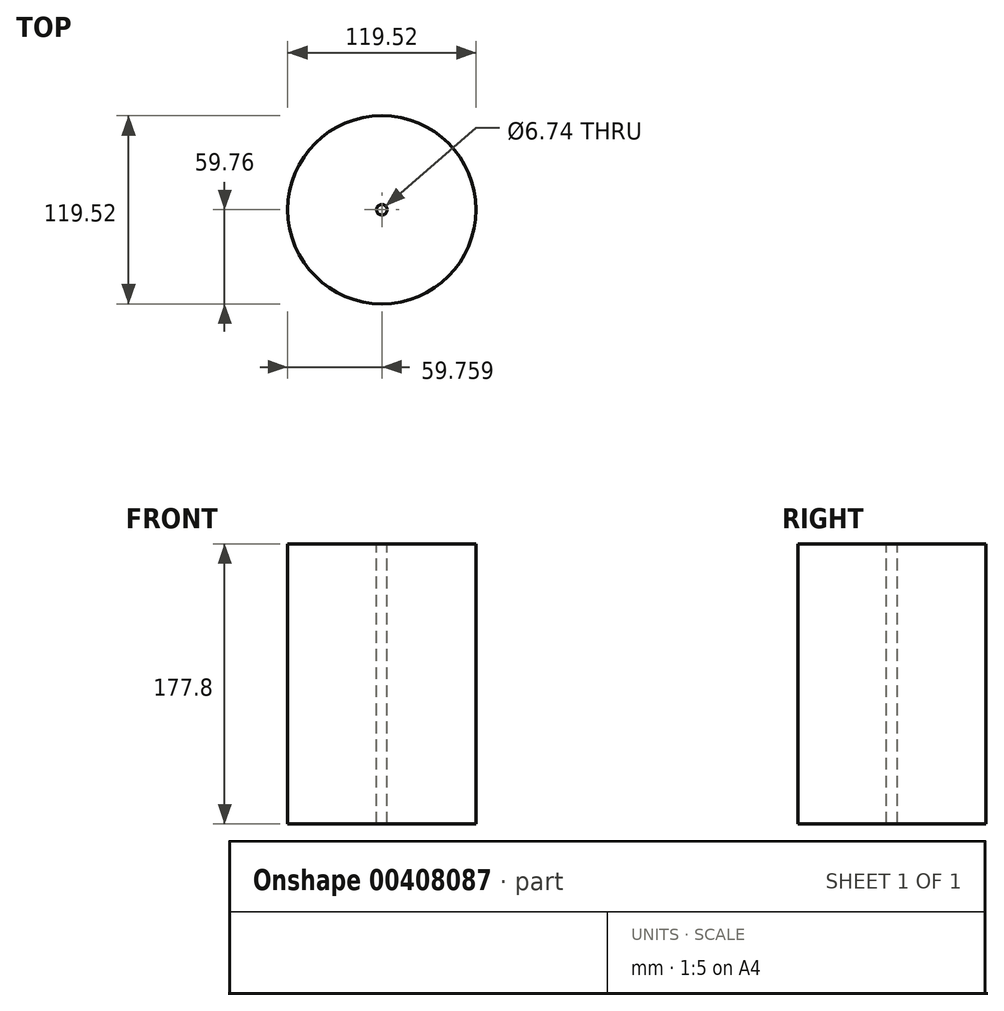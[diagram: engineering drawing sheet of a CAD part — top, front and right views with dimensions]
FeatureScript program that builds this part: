
annotation { "Feature Type Name" : "Feature", "Feature Type Description" : "" }
export const myFeature = defineFeature(function(context is Context, id is Id, definition is map)
    precondition{}
    {
        {
            var Q0;
            Q0=qCreatedBy(makeId("Front.planeOp"),FACE);
            var sketch = newSketch(context, id + "F0", { "sketchPlane" : qUnion([Q0])});
            skLineSegment(sketch, "E0.bottom", {"start": v(0, -69.44) * mm, "end": v(56.39, -69.44) * mm});
            skLineSegment(sketch, "E0.top", {"start": v(0, 59.35) * mm, "end": v(56.39, 59.35) * mm});
            skLineSegment(sketch, "E0.left", {"start": v(0, -69.44) * mm, "end": v(0, 59.35) * mm});
            skLineSegment(sketch, "E0.right", {"start": v(56.39, -69.44) * mm, "end": v(56.39, 59.35) * mm});
            skSolve(sketch);
        }
        {
            var Q0;
            Q0=qCreatedBy(makeId("Top.planeOp"),FACE);
            var sketch = newSketch(context, id + "F1", { "sketchPlane" : qUnion([Q0])});
            skCircle(sketch, "E1", {"center": v(59.76, 0) * mm, "radius": 59.76 * mm});
            skSolve(sketch);
        }
        {
            var Q0;
            Q0=sQuery(id+"F0.wireOp",EDGE,"E0.top");
            var Q1;
            Q1=sQuery(id+"F1.wireOp",EDGE,"E1");
            revolve(context, id + "F2", {"bodyType" : ToolBodyType.SURFACE, "surfaceEntities" : qUnion([Q0]), "axis" : qUnion([Q1]), "revolveType" : RevolveType.FULL});
        }
        {
            var Q0;
            Q0=makeQuery(id+"F2.opRevolve","SWEPT_FACE",FACE,{"disambiguationData":[OSD([sQuery(id+"F0.wireOp",EDGE,"E0.top")])]});
            extrude(context, id + "F3", {"entities" : qUnion([Q0]), "depth" : 177.8 * mm});
        }
    });
